# Revit family: Specialty_Equipment-Detroit_Radiant-Electric_Heater-ELX_Series-rev3
name_source: partatom
category: Specialty Equipment
units: mm (PartAtom-declared; Revit-internal decimal feet)

## family parameters
Always vertical = No
Cut with Voids When Loaded = No
Enable Cutting in Views = No
Maintain Annotation Orientation = No
OmniClass Number = 23.40.40.14
OmniClass Title = Food Service Equipment
Part Type = Normal
Room Calculation Point = No
Round Connector Dimension = Use Diameter
Shared = No
Work Plane-Based = Yes

## types (9) — shared parameters
Amperage = 0 A
CD_Material_Clearance Zone = Clearance-Detroit_Radiant-Shaded
CD_Material_Finish = Metal-Steel-Detroit_Radiant-Coated_Aluminized_Steel
CD_Prodcut Page URL = https://www.reverberray.com
CD_Product Documentation Link = https://www.reverberray.com
CD_Product Name = ELX-Series heaters
Description = Infrared Electric Heaters
Manufacturer = Detroit Radiant
Power Consumption = 0 VA
URL = https://www.reverberray.com
Voltage = 0 V
zero-valued in all types: Default Elevation

## per-type parameters (varying)
| type | CD_24X1 | CD_24X2 | CD_24X3 | CD_33X1 | CD_33X2 | CD_33X3 | CD_46X1 | CD_46X2 | CD_46X3 | CD_Heater Type | CD_Mounting Width | CD_W Clear | Model |
| ELX - 24" - Single | Yes | Yes | Yes | No | No | No | No | No | No | Specialty_Equipment-Detroit_Radiant-Unit_Nested_Heater-ELX_Series : ELX-24X1 | 23.5 " | 49 " | ELX-24X1 |
| ELX - 33" - Single | No | No | No | Yes | No | No | No | No | No | Specialty_Equipment-Detroit_Radiant-Unit_Nested_Heater-ELX_Series : ELX-33X1 | 32.5 " | 58 " | ELX-33X1 |
| ELX - 33" - Double | No | No | No | No | Yes | No | No | No | No | Specialty_Equipment-Detroit_Radiant-Unit_Nested_Heater-ELX_Series : ELX-33X2 | 32.5 " | 85 " | ELX-33X2 |
| ELX - 33" - Triple | No | No | No | No | No | Yes | No | No | No | Specialty_Equipment-Detroit_Radiant-Unit_Nested_Heater-ELX_Series : ELX-33X3 | 32.5 " | 102 " | ELX-33X3 |
| ELX - 46" - Single | No | No | No | No | No | No | Yes | No | No | Specialty_Equipment-Detroit_Radiant-Unit_Nested_Heater-ELX_Series : ELX-46X1 | 45.5 " | 71 " | ELX-46X1 |
| ELX - 46" - Double | No | No | No | No | No | No | No | Yes | No | Specialty_Equipment-Detroit_Radiant-Unit_Nested_Heater-ELX_Series : ELX-46X2 | 45.5 " | 99 " | ELX-46X2 |
| ELX - 46" - Triple | No | No | No | No | No | No | No | No | Yes | Specialty_Equipment-Detroit_Radiant-Unit_Nested_Heater-ELX_Series : ELX-46X3 | 45.5 " | 115 " | ELX-46X3 |
| ELX - 24" - Double | No | Yes | No | No | No | No | No | No | No | Specialty_Equipment-Detroit_Radiant-Unit_Nested_Heater-ELX_Series : ELX-24X1 | 23.5 " | 56 " | 0 |
| ELX - 24" - Triple | No | No | Yes | No | No | No | No | No | No | Specialty_Equipment-Detroit_Radiant-Unit_Nested_Heater-ELX_Series : ELX-24X1 | 23.5 " | 73 " | 0 |

## geometry (parser evidence)
native form markers: Sweep x8
no freeform markers — native parametric forms only
